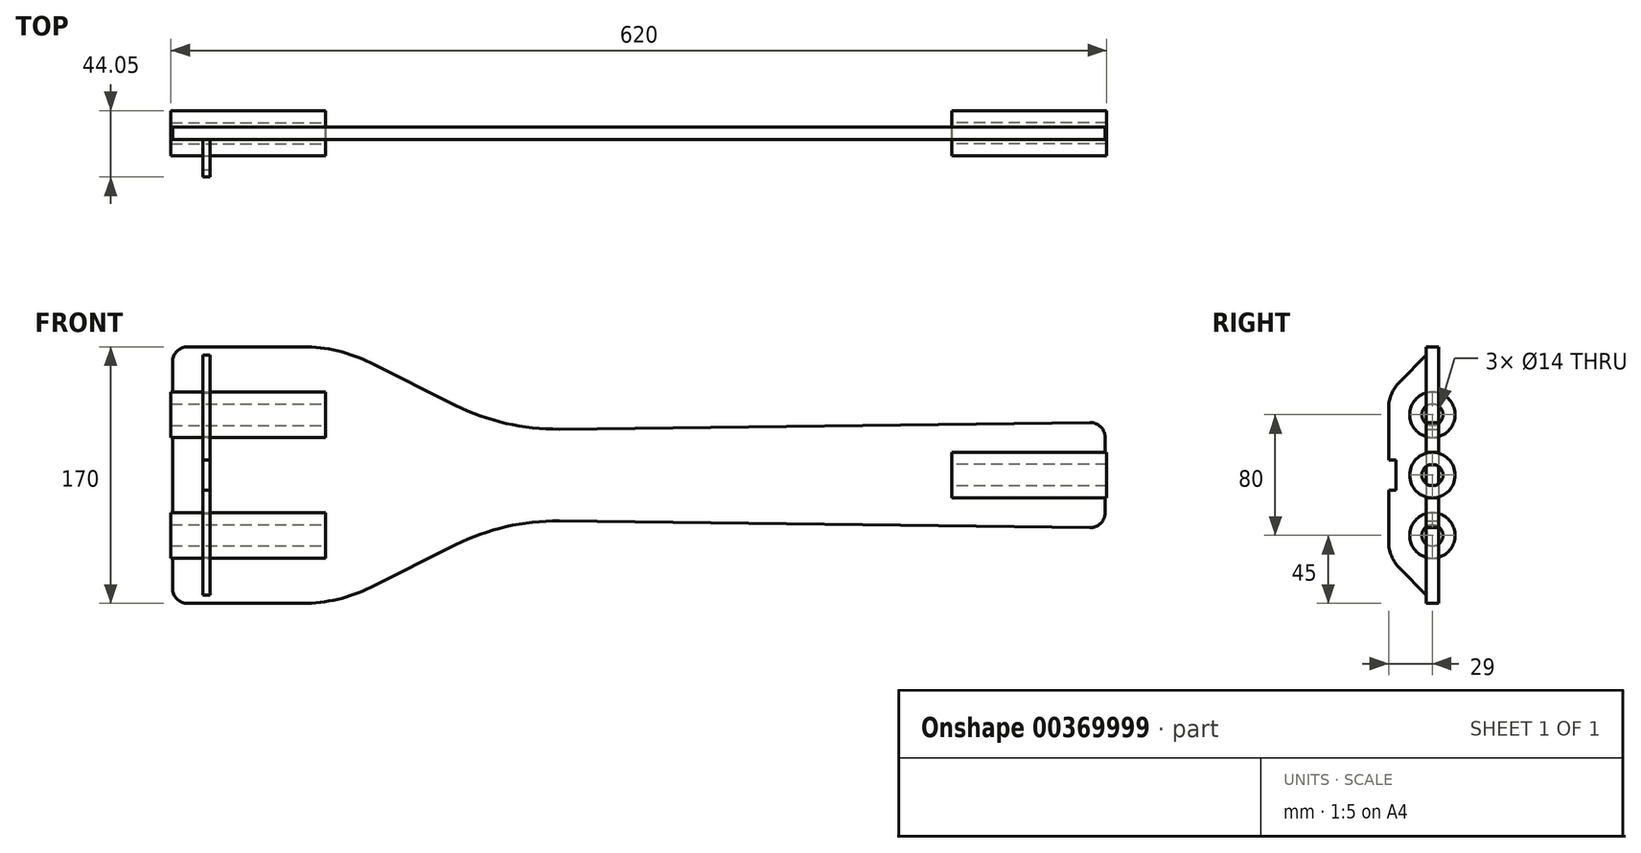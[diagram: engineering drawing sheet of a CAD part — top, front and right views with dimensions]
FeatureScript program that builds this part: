
annotation { "Feature Type Name" : "Feature", "Feature Type Description" : "" }
export const myFeature = defineFeature(function(context is Context, id is Id, definition is map)
    precondition{}
    {
        {
            var Q0;
            Q0=qCreatedBy(makeId("Front.planeOp"),FACE);
            var sketch = newSketch(context, id + "F0", { "sketchPlane" : qUnion([Q0])});
            skCircle(sketch, "E0", {"center": v(0, 0) * mm, "radius": 26.75 * mm});
            skCircle(sketch, "E1", {"center": v(0, 0) * mm, "radius": 32.5 * mm});
            skLineSegment(sketch, "E2", {"start": v(-31.74, 7) * mm, "end": v(-130, 7) * mm});
            skLineSegment(sketch, "E3", {"start": v(-130, 7) * mm, "end": v(-130, -7) * mm});
            skLineSegment(sketch, "E4", {"start": v(-130, -7) * mm, "end": v(-31.74, -7) * mm});
            skCircle(sketch, "E5", {"center": v(-850, 0) * mm, "radius": 32.5 * mm});
            skPoint(sketch, "E6", {"position": v(-130, 0) * mm});
            skCircle(sketch, "E7", {"center": v(-725, 40) * mm, "radius": 32.5 * mm});
            skCircle(sketch, "E8", {"center": v(-725, 40) * mm, "radius": 26.75 * mm});
            skLineSegment(sketch, "E9", {"start": v(-595, 47) * mm, "end": v(-595, 33) * mm});
            skLineSegment(sketch, "E10", {"start": v(-595, 33) * mm, "end": v(-693.26, 33) * mm});
            skPoint(sketch, "E11", {"position": v(-595, 40) * mm});
            skLineSegment(sketch, "E12.trimOffspring", {"start": v(-693.26, 47) * mm, "end": v(-595, 47) * mm});
            skLineSegment(sketch, "E13.bottom", {"start": v(-52.5, 15) * mm, "end": v(-155, 15) * mm, "construction": true});
            skLineSegment(sketch, "E13.top", {"start": v(-52.5, -15) * mm, "end": v(-155, -15) * mm, "construction": true});
            skLineSegment(sketch, "E13.left", {"start": v(-52.5, 15) * mm, "end": v(-52.5, -15) * mm, "construction": true});
            skLineSegment(sketch, "E13.right", {"start": v(-155, 15) * mm, "end": v(-155, -15) * mm, "construction": true});
            skPoint(sketch, "E14", {"position": v(-155, 0) * mm});
            skLineSegment(sketch, "E15.bottom", {"start": v(-672.5, 55) * mm, "end": v(-570, 55) * mm, "construction": true});
            skLineSegment(sketch, "E15.top", {"start": v(-672.5, 25) * mm, "end": v(-570, 25) * mm, "construction": true});
            skLineSegment(sketch, "E15.left", {"start": v(-672.5, 55) * mm, "end": v(-672.5, 25) * mm, "construction": true});
            skLineSegment(sketch, "E15.right", {"start": v(-570, 55) * mm, "end": v(-570, 25) * mm, "construction": true});
            skPoint(sketch, "E16", {"position": v(-570, 40) * mm});
            skCircle(sketch, "E17", {"center": v(-725, -40) * mm, "radius": 26.75 * mm});
            skCircle(sketch, "E18", {"center": v(-725, -40) * mm, "radius": 32.5 * mm});
            skLineSegment(sketch, "E19", {"start": v(-693.26, -33) * mm, "end": v(-595, -33) * mm});
            skLineSegment(sketch, "E20", {"start": v(-595, -33) * mm, "end": v(-595, -47) * mm});
            skLineSegment(sketch, "E21", {"start": v(-595, -47) * mm, "end": v(-693.26, -47) * mm});
            skPoint(sketch, "E22", {"position": v(-595, -40) * mm});
            skSolve(sketch);
        }
        {
            var Q0;
            Q0=qCreatedBy(makeId("Front.planeOp"),FACE);
            var sketch = newSketch(context, id + "F1", { "sketchPlane" : qUnion([Q0])});
            skLineSegment(sketch, "E23", {"start": v(-53.5, 15) * mm, "end": v(-53.5, 24.87) * mm});
            skLineSegment(sketch, "E24", {"start": v(-53.5, -35) * mm, "end": v(-671.5, -85) * mm, "construction": true});
            skLineSegment(sketch, "E25", {"start": v(-671.5, 55) * mm, "end": v(-671.5, 75) * mm});
            skLineSegment(sketch, "E26", {"start": v(-671.5, 25) * mm, "end": v(-671.5, -25) * mm});
            skLineSegment(sketch, "E27", {"start": v(-671.5, 85) * mm, "end": v(-53.5, 35) * mm, "construction": true});
            skLineSegment(sketch, "E28", {"start": v(-671.5, 55) * mm, "end": v(-570, 55) * mm});
            skLineSegment(sketch, "E29", {"start": v(-570, 55) * mm, "end": v(-570, 25) * mm});
            skLineSegment(sketch, "E30", {"start": v(-570, 25) * mm, "end": v(-671.5, 25) * mm});
            skLineSegment(sketch, "E31", {"start": v(-671.5, -25) * mm, "end": v(-570, -25) * mm});
            skLineSegment(sketch, "E32", {"start": v(-570, -25) * mm, "end": v(-570, -55) * mm});
            skLineSegment(sketch, "E33", {"start": v(-570, -55) * mm, "end": v(-671.5, -55) * mm});
            skPoint(sketch, "E34", {"position": v(-570, -40) * mm});
            skLineSegment(sketch, "E35.bottom", {"start": v(-53.5, 15) * mm, "end": v(-155, 15) * mm});
            skLineSegment(sketch, "E35.top", {"start": v(-53.5, -15) * mm, "end": v(-155, -15) * mm});
            skLineSegment(sketch, "E35.right", {"start": v(-155, 15) * mm, "end": v(-155, -15) * mm});
            skPoint(sketch, "E36.visualSharp", {"position": v(-671.5, 85) * mm});
            skPoint(sketch, "E37.visualSharp", {"position": v(-671.5, -85) * mm});
            skPoint(sketch, "E38.visualSharp", {"position": v(-53.5, -35) * mm});
            skPoint(sketch, "E39.visualSharp", {"position": v(-53.5, 35) * mm});
            skLineSegment(sketch, "E40", {"start": v(-53.5, -15) * mm, "end": v(-53.5, -24.87) * mm});
            skLineSegment(sketch, "E41", {"start": v(-671.5, -55) * mm, "end": v(-671.5, -75) * mm});
            skLineSegment(sketch, "E42", {"start": v(-63.63, 34.87) * mm, "end": v(-415.1, 30.46) * mm});
            skLineSegment(sketch, "E43", {"start": v(-63.63, -34.87) * mm, "end": v(-415.1, -30.46) * mm});
            skLineSegment(sketch, "E44", {"start": v(-661.5, 85) * mm, "end": v(-585.1, 85) * mm});
            skLineSegment(sketch, "E45", {"start": v(-540.39, 74.44) * mm, "end": v(-484.06, 46.28) * mm});
            skLineSegment(sketch, "E46", {"start": v(-661.5, -85) * mm, "end": v(-585.1, -85) * mm});
            skLineSegment(sketch, "E47", {"start": v(-540.39, -74.44) * mm, "end": v(-484.06, -46.28) * mm});
            skLineSegment(sketch, "E48", {"start": v(-451.5, 30) * mm, "end": v(-451.5, -30) * mm, "construction": true});
            skPoint(sketch, "E49", {"position": v(-451.5, 0) * mm});
            skPoint(sketch, "E50.visualSharp", {"position": v(-451.5, 30) * mm});
            skArc(sketch, "E50.filletArc", {"start": v(-484.06, 46.28) * mm, "mid": v(-450.53, 34.24) * mm, "end": v(-415.1, 30.46) * mm});
            skPoint(sketch, "E51.visualSharp", {"position": v(-561.5, 85) * mm});
            skArc(sketch, "E51.filletArc", {"start": v(-540.39, 74.44) * mm, "mid": v(-562.13, 82.32) * mm, "end": v(-585.1, 85) * mm});
            skPoint(sketch, "E52.visualSharp", {"position": v(-561.5, -85) * mm});
            skArc(sketch, "E52.filletArc", {"start": v(-585.1, -85) * mm, "mid": v(-562.13, -82.32) * mm, "end": v(-540.39, -74.44) * mm});
            skPoint(sketch, "E53.visualSharp", {"position": v(-451.5, -30) * mm});
            skArc(sketch, "E53.filletArc", {"start": v(-415.1, -30.46) * mm, "mid": v(-450.53, -34.24) * mm, "end": v(-484.06, -46.28) * mm});
            skArc(sketch, "E54.filletArc", {"start": v(-661.5, 85) * mm, "mid": v(-668.57, 82.07) * mm, "end": v(-671.5, 75) * mm});
            skArc(sketch, "E55.filletArc", {"start": v(-671.5, -75) * mm, "mid": v(-668.57, -82.07) * mm, "end": v(-661.5, -85) * mm});
            skArc(sketch, "E56.filletArc", {"start": v(-63.63, -34.87) * mm, "mid": v(-56.47, -31.99) * mm, "end": v(-53.5, -24.87) * mm});
            skArc(sketch, "E57.filletArc", {"start": v(-53.5, 24.87) * mm, "mid": v(-56.47, 31.99) * mm, "end": v(-63.63, 34.87) * mm});
            skSolve(sketch);
        }
        {
            var Q0;
            Q0 = qSketchRegion(id + "F1", true);
            extrude(context, id + "F2", {"entities" : qUnion([Q0]), "depth" : 8 * mm});
        }
        {
            var Q0;
            Q0=makeQuery(id+"F2.opExtrude","SWEPT_FACE",FACE,{"disambiguationData":[OSD([sQuery(id+"F1.wireOp",EDGE,"E35.right")])]});
            var sketch = newSketch(context, id + "F3", { "sketchPlane" : qUnion([Q0])});
            skCircle(sketch, "E58", {"center": v(-4, 0) * mm, "radius": 7 * mm});
            skCircle(sketch, "E59", {"center": v(-4, 0) * mm, "radius": 15.05 * mm});
            skSolve(sketch);
        }
        {
            var Q0;
            Q0 = qSketchRegion(id + "F3", true);
            extrude(context, id + "F4", {"entities" : qUnion([Q0]), "depth" : 102.5 * mm});
        }
        {
            var Q0;
            Q0=makeQuery(id+"F2.opExtrude","SWEPT_FACE",FACE,{"disambiguationData":[OSD([sQuery(id+"F1.wireOp",EDGE,"E29")])]});
            var sketch = newSketch(context, id + "F5", { "sketchPlane" : qUnion([Q0])});
            skCircle(sketch, "E60", {"center": v(4, 40) * mm, "radius": 15.05 * mm});
            skPoint(sketch, "E60.centerSnap0", {"position": v(0, 40) * mm});
            skCircle(sketch, "E61", {"center": v(4, 40) * mm, "radius": 7 * mm});
            skCircle(sketch, "E62", {"center": v(4, -40) * mm, "radius": 7 * mm});
            skCircle(sketch, "E63", {"center": v(4, -40) * mm, "radius": 15.05 * mm});
            skSolve(sketch);
        }
        {
            var Q0;
            Q0 = qSketchRegion(id + "F5", true);
            extrude(context, id + "F6", {"entities" : qUnion([Q0]), "depth" : 102.5 * mm});
        }
        {
            var Q0;
            Q0=makeQuery(id+"F2.opExtrude","SWEPT_FACE",FACE,{"disambiguationData":[OSD([sQuery(id+"F1.wireOp",EDGE,"E26")])]});
            cPlane(context, id + "F7", {"entities" : qUnion([Q0]), "cplaneType" : CPlaneType.OFFSET, "offset" : 25 * mm, "oppositeDirection" : true, "width" : 150 * mm, "height" : 150 * mm});
        }
        {
            var Q0;
            Q0=qCreatedBy(id+"F7.planeOp",FACE);
            var sketch = newSketch(context, id + "F8", { "sketchPlane" : qUnion([Q0])});
            skLineSegment(sketch, "E64", {"start": v(8, 79.46) * mm, "end": v(25.68, 61.78) * mm});
            skLineSegment(sketch, "E65", {"start": v(33, 44.1) * mm, "end": v(33, 10) * mm});
            skLineSegment(sketch, "E66", {"start": v(25.68, -61.78) * mm, "end": v(8, -79.46) * mm});
            skLineSegment(sketch, "E67", {"start": v(8, -79.46) * mm, "end": v(8, -54.46) * mm});
            skLineSegment(sketch, "E68", {"start": v(8, 79.46) * mm, "end": v(8, 54.46) * mm});
            skArc(sketch, "E69", {"start": v(8, 25.54) * mm, "mid": v(19, 40) * mm, "end": v(8, 54.46) * mm});
            skArc(sketch, "E70", {"start": v(8, -54.46) * mm, "mid": v(19, -40) * mm, "end": v(8, -25.54) * mm});
            skLineSegment(sketch, "E71", {"start": v(8, 25.54) * mm, "end": v(8, -25.54) * mm});
            skPoint(sketch, "E72.visualSharp", {"position": v(33, 54.46) * mm});
            skArc(sketch, "E72.filletArc", {"start": v(33, 44.1) * mm, "mid": v(31.1, 53.67) * mm, "end": v(25.68, 61.78) * mm});
            skPoint(sketch, "E73.visualSharp", {"position": v(33, -54.46) * mm});
            skArc(sketch, "E73.filletArc", {"start": v(25.68, -61.78) * mm, "mid": v(31.1, -53.67) * mm, "end": v(33, -44.1) * mm});
            skLineSegment(sketch, "E74.bottom", {"start": v(33, 10) * mm, "end": v(28, 10) * mm});
            skLineSegment(sketch, "E74.top", {"start": v(33, -10) * mm, "end": v(28, -10) * mm});
            skLineSegment(sketch, "E74.right", {"start": v(28, 10) * mm, "end": v(28, -10) * mm});
            skLineSegment(sketch, "E75.trimOffspring", {"start": v(33, -10) * mm, "end": v(33, -44.1) * mm});
            skSolve(sketch);
        }
        {
            var Q0;
            Q0 = qSketchRegion(id + "F8", true);
            extrude(context, id + "F9", {"entities" : qUnion([Q0]), "depth" : 5 * mm});
        }
    });
